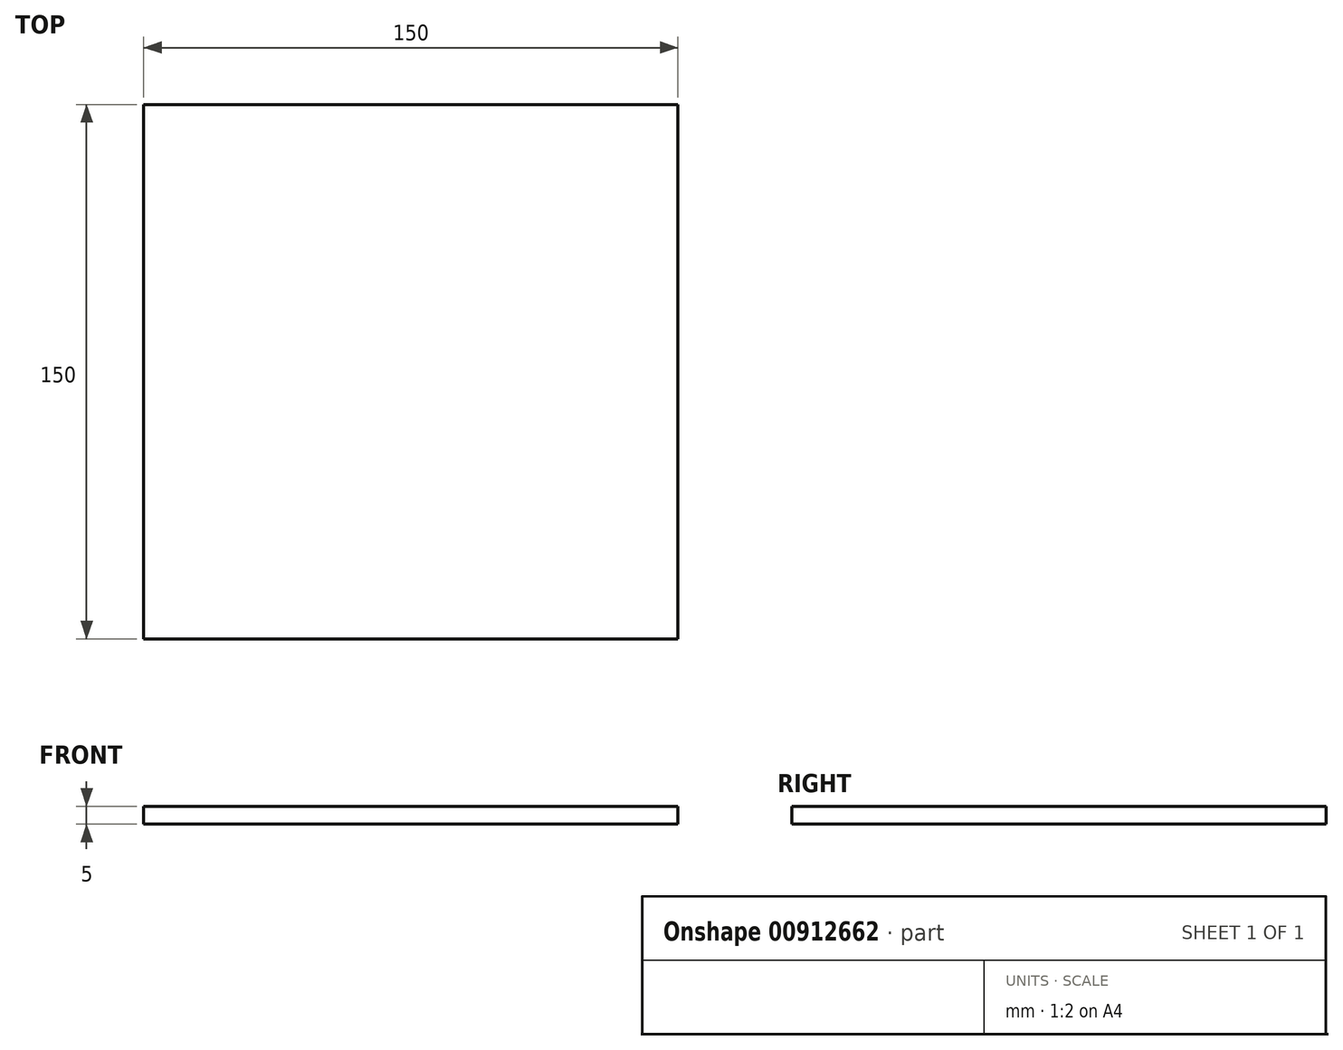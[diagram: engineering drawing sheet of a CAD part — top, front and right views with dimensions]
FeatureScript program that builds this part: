
annotation { "Feature Type Name" : "Feature", "Feature Type Description" : "" }
export const myFeature = defineFeature(function(context is Context, id is Id, definition is map)
    precondition{}
    {
        {
            var Q0;
            Q0=qCreatedBy(makeId("Top.planeOp"),FACE);
            var sketch = newSketch(context, id + "F0", { "sketchPlane" : qUnion([Q0])});
            skLineSegment(sketch, "E0.bottom", {"start": v(-75, 75) * mm, "end": v(75, 75) * mm});
            skLineSegment(sketch, "E0.top", {"start": v(-75, -75) * mm, "end": v(75, -75) * mm});
            skLineSegment(sketch, "E0.left", {"start": v(-75, 75) * mm, "end": v(-75, -75) * mm});
            skLineSegment(sketch, "E0.right", {"start": v(75, 75) * mm, "end": v(75, -75) * mm});
            skPoint(sketch, "E0.middle", {"position": v(0, 0) * mm});
            skSolve(sketch);
        }
        {
            var Q0;
            Q0 = qSketchRegion(id + "F0", true);
            extrude(context, id + "F1", {"entities" : qUnion([Q0]), "depth" : 5 * mm, "offsetDistance" : 25 * mm});
        }
    });
